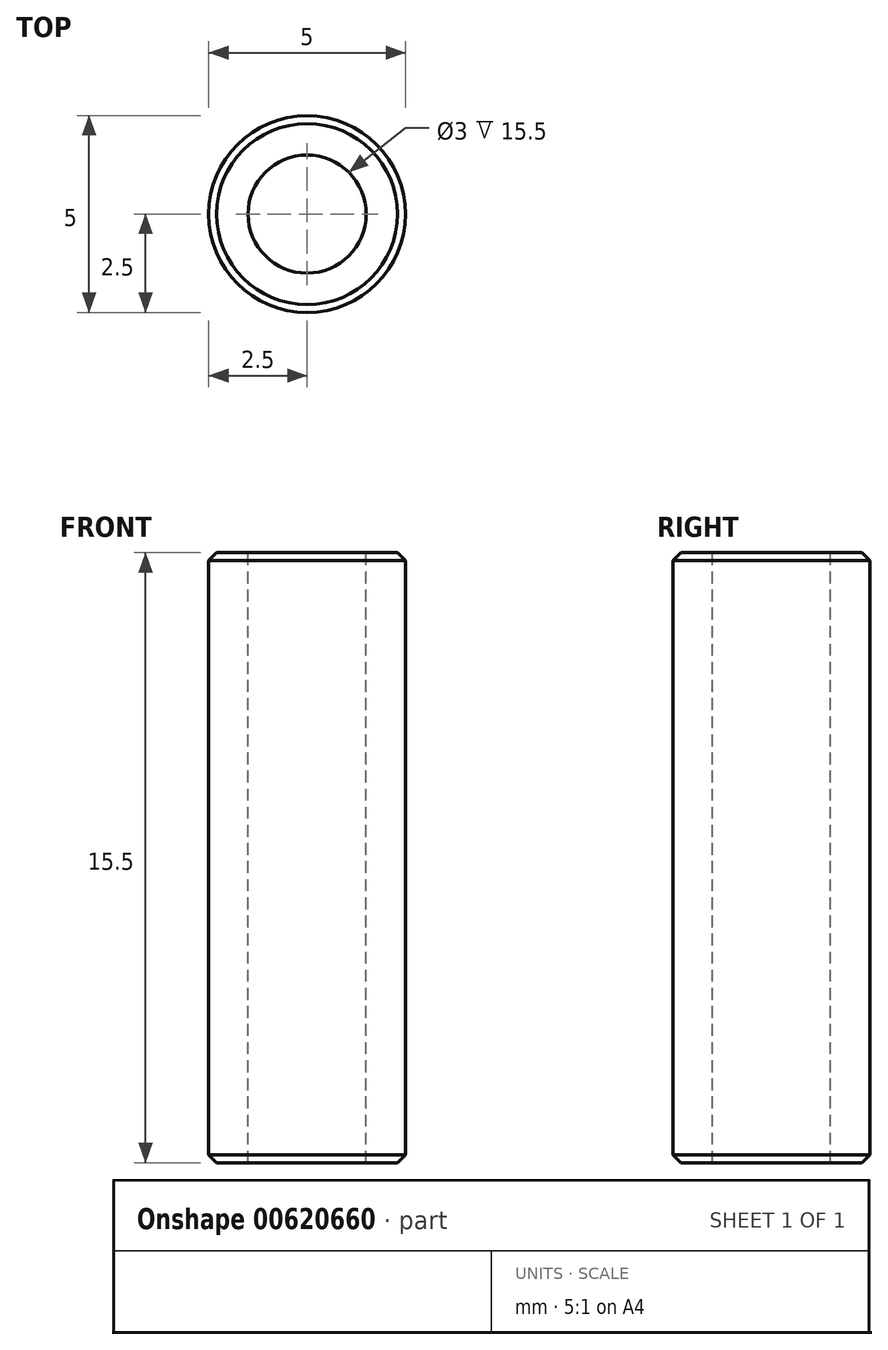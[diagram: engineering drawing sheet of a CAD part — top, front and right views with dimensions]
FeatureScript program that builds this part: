
annotation { "Feature Type Name" : "Feature", "Feature Type Description" : "" }
export const myFeature = defineFeature(function(context is Context, id is Id, definition is map)
    precondition{}
    {
        {
            var Q0;
            Q0=qCreatedBy(makeId("Top.planeOp"),FACE);
            var sketch = newSketch(context, id + "F0", { "sketchPlane" : qUnion([Q0])});
            skCircle(sketch, "E0", {"center": v(0, 0) * mm, "radius": 2.5 * mm});
            skSolve(sketch);
        }
        {
            var Q0;
            Q0=qSketchRegion(id+"F0",true);
            extrude(context, id + "F1", {"entities" : qUnion([Q0]), "depth" : 15.5 * mm, "offsetDistance" : 25 * mm});
        }
        {
            var Q0;
            Q0=makeQuery(id+"F1.opExtrude","CAP_FACE",FACE,{"disambiguationData":[OSD([sQuery(id+"F0.wireOp",EDGE,"E0")])],"isStart":false});
            var Q1;
            Q1=makeQuery(id+"F1.opExtrude","CAP_FACE",FACE,{"disambiguationData":[OSD([sQuery(id+"F0.wireOp",EDGE,"E0")])],"isStart":true});
            chamfer(context, id + "F2", {"entities" : qUnion([Q0, Q1]), "width" : 0.2 * mm, "tangentPropagation" : true});
        }
        {
            var Q0;
            Q0=sQuery(id+"F0.wireOp",VERTEX,"E0.center");
            var Q1;
            Q1=makeQuery(id+"F1.opExtrude","SWEPT_BODY",BODY,{"disambiguationData":[OSD([sQuery(id+"F0.wireOp",EDGE,"E0")])]});
            hole(context, id + "F3", {"style" : HoleStyle.SIMPLE, "endStyle" : HoleEndStyle.THROUGH, "oppositeDirection" : true, "holeDiameter" : 3 * mm, "isTappedThrough" : true, "tappedDepth" : 12 * mm, "tapClearance" : 3, "locations" : qUnion([Q0]), "scope" : qUnion([Q1]), "startStyle" : HoleStartStyle.SKETCH});
        }
    });
